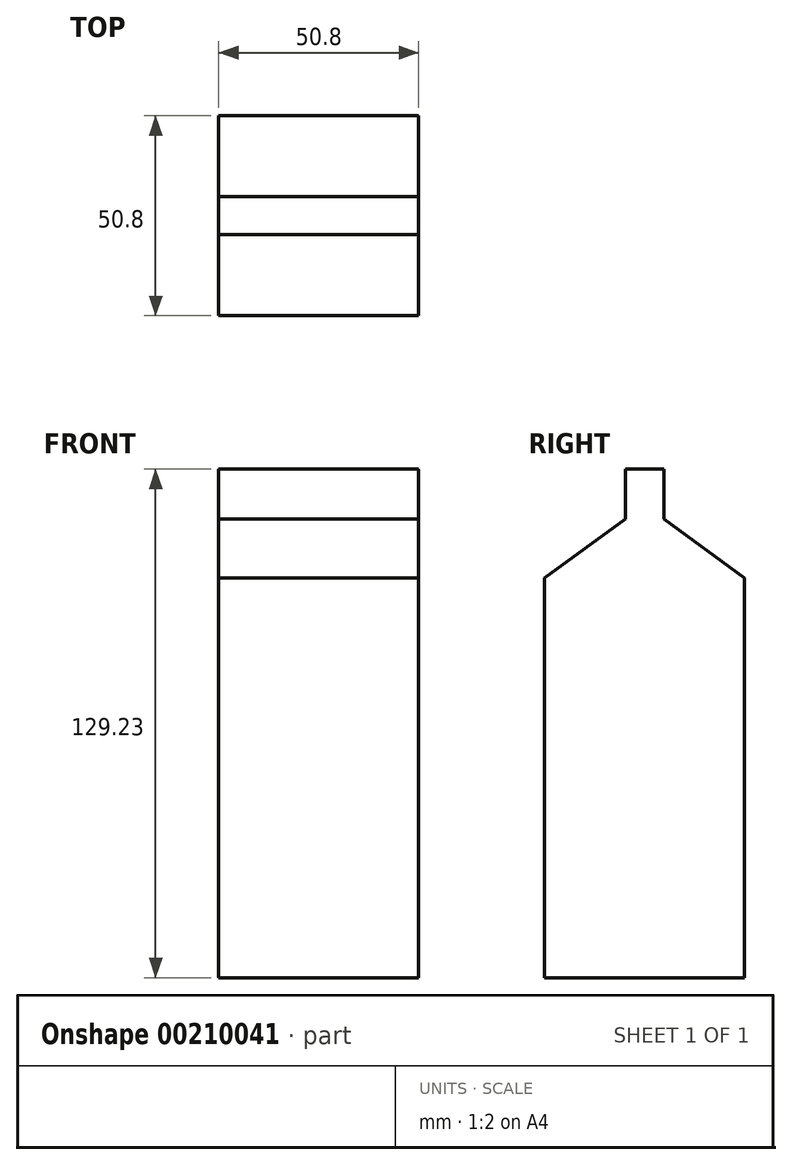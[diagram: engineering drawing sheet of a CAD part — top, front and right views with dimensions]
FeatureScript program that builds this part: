
annotation { "Feature Type Name" : "Feature", "Feature Type Description" : "" }
export const myFeature = defineFeature(function(context is Context, id is Id, definition is map)
    precondition{}
    {
        {
            var Q0;
            Q0=qCreatedBy(makeId("Right.planeOp"),FACE);
            var sketch = newSketch(context, id + "F0", { "sketchPlane" : qUnion([Q0])});
            skLineSegment(sketch, "E0.top", {"start": v(-25.4, -98.67) * mm, "end": v(25.4, -98.67) * mm});
            skLineSegment(sketch, "E0.left", {"start": v(-25.4, 2.93) * mm, "end": v(-25.4, -98.67) * mm});
            skLineSegment(sketch, "E0.right", {"start": v(25.4, 2.93) * mm, "end": v(25.4, -98.67) * mm});
            skPoint(sketch, "E0.middle", {"position": v(0, -47.87) * mm});
            skLineSegment(sketch, "E1", {"start": v(25.4, 0) * mm, "end": v(25.4, 2.93) * mm});
            skLineSegment(sketch, "E2", {"start": v(25.4, 2.93) * mm, "end": v(4.85, 17.86) * mm});
            skLineSegment(sketch, "E3", {"start": v(4.85, 17.86) * mm, "end": v(4.85, 30.56) * mm});
            skLineSegment(sketch, "E4", {"start": v(4.85, 30.56) * mm, "end": v(0, 30.56) * mm});
            skLineSegment(sketch, "E5.MirrorCS", {"start": v(-4.85, 30.56) * mm, "end": v(0, 30.56) * mm});
            skLineSegment(sketch, "E6.MirrorCS", {"start": v(-25.4, 2.93) * mm, "end": v(-4.85, 17.86) * mm});
            skLineSegment(sketch, "E7.MirrorCS", {"start": v(-4.85, 17.86) * mm, "end": v(-4.85, 30.56) * mm});
            skSolve(sketch);
        }
        {
            var Q0;
            Q0 = qSketchRegion(id + "F0", true);
            extrude(context, id + "F1", {"entities" : qUnion([Q0]), "depth" : 25.4 * mm, "hasSecondDirection" : true, "secondDirectionOppositeDirection" : true, "secondDirectionDepth" : 25.4 * mm});
        }
    });
